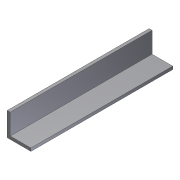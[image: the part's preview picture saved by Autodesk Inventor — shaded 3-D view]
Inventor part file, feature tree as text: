
AUTODESK INVENTOR PART (.ipt)
format: ipt  version: 2012 (Build 160160000, 160)  size: 72,704 bytes
history: native  units: in
note: dims shown in document units (in); Inventor stores cm internally (conversion verified against a paired STEP export)
features: extrude x1, sketch x1
ambient origin geometry x8: Origin, YZ Plane, XZ Plane, XY Plane, X Axis, Y Axis, Z Axis, Center Point
bodies: Solid1 (feature_tree)
feature tree (2):
  extrude  "Extrusion1"  Depth=0.125in
  sketch  "Sketch1"  dims[d0=1.0in d1=0.125in d2=6.0in d3=0.0in]
